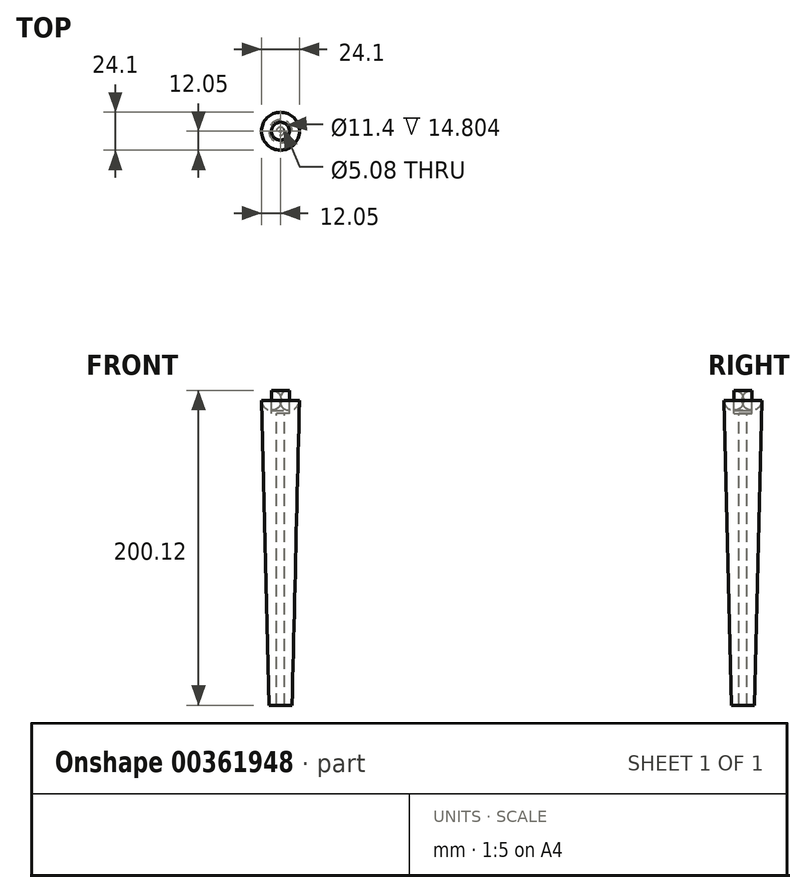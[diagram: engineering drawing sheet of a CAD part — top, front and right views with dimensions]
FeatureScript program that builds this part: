
annotation { "Feature Type Name" : "Feature", "Feature Type Description" : "" }
export const myFeature = defineFeature(function(context is Context, id is Id, definition is map)
    precondition{}
    {
        {
            var Q0;
            Q0=qCreatedBy(makeId("Front.planeOp"),FACE);
            var sketch = newSketch(context, id + "F0", { "sketchPlane" : qUnion([Q0])});
            skLineSegment(sketch, "E0", {"start": v(12.05, 95.45) * mm, "end": v(7.37, -98.16) * mm});
            skLineSegment(sketch, "E1", {"start": v(7.37, -98.16) * mm, "end": v(2.54, -98.04) * mm});
            skLineSegment(sketch, "E2", {"start": v(2.54, -98.04) * mm, "end": v(2.54, 87.15) * mm});
            skArc(sketch, "E3.filletArc", {"start": v(12.05, 95.45) * mm, "mid": v(10.24, 100.04) * mm, "end": v(5.7, 101.96) * mm});
            skLineSegment(sketch, "E4", {"start": v(5.7, 101.96) * mm, "end": v(5.7, 87.15) * mm});
            skLineSegment(sketch, "E5", {"start": v(5.7, 87.15) * mm, "end": v(2.54, 87.15) * mm});
            skSolve(sketch);
        }
        {
            var Q0;
            Q0=qCreatedBy(makeId("Front.planeOp"),FACE);
            var sketch = newSketch(context, id + "F1", { "sketchPlane" : qUnion([Q0])});
            skLineSegment(sketch, "E6", {"start": v(0, 107.53) * mm, "end": v(0, -98.86) * mm, "construction": true});
            skSolve(sketch);
        }
        {
            var Q0;
            Q0 = qSketchRegion(id + "F0", true);
            var Q1;
            Q1=sQuery(id+"F1.wireOp",EDGE,"E6");
            revolve(context, id + "F2", {"entities" : qUnion([Q0]), "axis" : qUnion([Q1]), "revolveType" : RevolveType.FULL});
        }
    });
